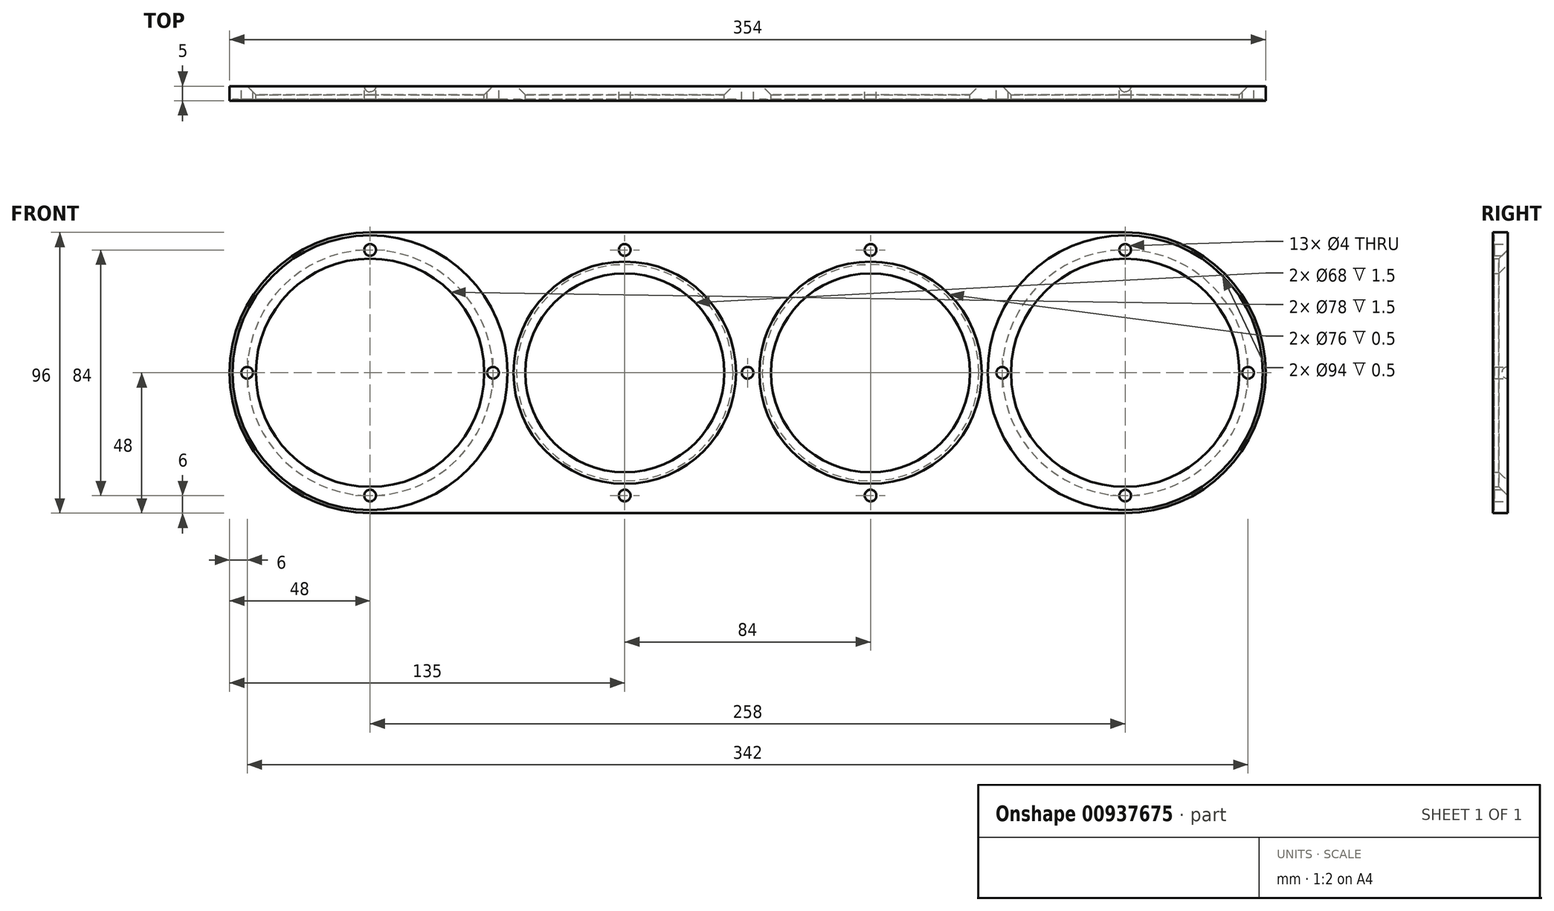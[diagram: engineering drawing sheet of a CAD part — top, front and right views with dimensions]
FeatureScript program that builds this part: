
annotation { "Feature Type Name" : "Feature", "Feature Type Description" : "" }
export const myFeature = defineFeature(function(context is Context, id is Id, definition is map)
    precondition{}
    {
        {
            var Q0;
            Q0=qCreatedBy(makeId("Front.planeOp"),FACE);
            var sketch = newSketch(context, id + "F0", { "sketchPlane" : qUnion([Q0])});
            skCircle(sketch, "E0", {"center": v(42, 0) * mm, "radius": 34 * mm});
            skCircle(sketch, "E1", {"center": v(129, 0) * mm, "radius": 39 * mm});
            skLineSegment(sketch, "E2", {"start": v(0, -113.77) * mm, "end": v(0, 113.17) * mm, "construction": true});
            skArc(sketch, "E3", {"start": v(129, 48) * mm, "mid": v(177, 0) * mm, "end": v(129, -48) * mm});
            skLineSegment(sketch, "E4", {"start": v(129, -48) * mm, "end": v(0, -48) * mm});
            skLineSegment(sketch, "E5", {"start": v(129, 48) * mm, "end": v(0, 48) * mm});
            skLineSegment(sketch, "E6.MirrorCS", {"start": v(-129, -48) * mm, "end": v(0, -48) * mm});
            skLineSegment(sketch, "E7.MirrorCS", {"start": v(-129, 48) * mm, "end": v(0, 48) * mm});
            skArc(sketch, "E8.MirrorCS", {"start": v(-129, 48) * mm, "mid": v(-177, 0) * mm, "end": v(-129, -48) * mm});
            skCircle(sketch, "E9.MirrorC", {"center": v(-129, 0) * mm, "radius": 39 * mm});
            skCircle(sketch, "E10.MirrorC", {"center": v(-42, 0) * mm, "radius": 34 * mm});
            skCircle(sketch, "E11", {"center": v(129, 42) * mm, "radius": 2 * mm});
            skCircle(sketch, "E12.1.0", {"center": v(87, 0) * mm, "radius": 2 * mm});
            skCircle(sketch, "E12.2.0", {"center": v(129, -42) * mm, "radius": 2 * mm});
            skCircle(sketch, "E12.3.0", {"center": v(171, 0) * mm, "radius": 2 * mm});
            skCircle(sketch, "E13.MirrorC", {"center": v(-171, 0) * mm, "radius": 2 * mm});
            skCircle(sketch, "E14.MirrorC", {"center": v(-129, 42) * mm, "radius": 2 * mm});
            skCircle(sketch, "E15.MirrorC", {"center": v(-129, -42) * mm, "radius": 2 * mm});
            skCircle(sketch, "E16.MirrorC", {"center": v(-87, 0) * mm, "radius": 2 * mm});
            skCircle(sketch, "E17", {"center": v(42, 42) * mm, "radius": 2 * mm});
            skCircle(sketch, "E18.1.0", {"center": v(42, -42) * mm, "radius": 2 * mm});
            skCircle(sketch, "E19.MirrorC", {"center": v(-42, 42) * mm, "radius": 2 * mm});
            skCircle(sketch, "E20.MirrorC", {"center": v(-42, -42) * mm, "radius": 2 * mm});
            skCircle(sketch, "E21", {"center": v(0, 0) * mm, "radius": 2 * mm});
            skSolve(sketch);
        }
        {
            var Q0;
            Q0=qSketchRegion(id+"F0",true);
            extrude(context, id + "F1", {"entities" : qUnion([Q0]), "depth" : 5 * mm, "offsetDistance" : 25 * mm});
        }
        {
            var Q0;
            Q0=makeQuery(id+"F1.opExtrude","CAP_FACE",FACE,{"disambiguationData":[OSD([sQuery(id+"F0.wireOp",EDGE,"E0"),sQuery(id+"F0.wireOp",EDGE,"E1"),sQuery(id+"F0.wireOp",EDGE,"E3"),sQuery(id+"F0.wireOp",EDGE,"E4"),sQuery(id+"F0.wireOp",EDGE,"E5"),sQuery(id+"F0.wireOp",EDGE,"E6.MirrorCS"),sQuery(id+"F0.wireOp",EDGE,"E7.MirrorCS"),sQuery(id+"F0.wireOp",EDGE,"E8.MirrorCS"),sQuery(id+"F0.wireOp",EDGE,"E9.MirrorC"),sQuery(id+"F0.wireOp",EDGE,"E10.MirrorC")])],"isStart":false});
            var sketch = newSketch(context, id + "F2", { "sketchPlane" : qUnion([Q0])});
            skCircle(sketch, "E22", {"center": v(42, 0) * mm, "radius": 38 * mm});
            skCircle(sketch, "E23.MirrorC", {"center": v(-42, 0) * mm, "radius": 38 * mm});
            skCircle(sketch, "E24", {"center": v(129, 0) * mm, "radius": 47 * mm});
            skCircle(sketch, "E25.MirrorC", {"center": v(-129, 0) * mm, "radius": 47 * mm});
            skSolve(sketch);
        }
        {
            var Q0;
            Q0 = qSketchRegion(id + "F2", true);
            extrude(context, id + "F3", {"entities" : qUnion([Q0]), "operationType" : NewBodyOperationType.REMOVE, "oppositeDirection" : true, "depth" : 0.5 * mm, "offsetDistance" : 25 * mm});
        }
        {
            var Q0;
            Q0=makeQuery(id+"F1.opExtrude","CAP_EDGE",EDGE,{"disambiguationData":[OSD([sQuery(id+"F0.wireOp",EDGE,"E9.MirrorC")])],"isStart":true});
            var Q1;
            Q1=makeQuery(id+"F1.opExtrude","CAP_EDGE",EDGE,{"disambiguationData":[OSD([sQuery(id+"F0.wireOp",EDGE,"E10.MirrorC")])],"isStart":true});
            var Q2;
            Q2=makeQuery(id+"F1.opExtrude","CAP_EDGE",EDGE,{"disambiguationData":[OSD([sQuery(id+"F0.wireOp",EDGE,"E0")])],"isStart":true});
            var Q3;
            Q3=makeQuery(id+"F1.opExtrude","CAP_EDGE",EDGE,{"disambiguationData":[OSD([sQuery(id+"F0.wireOp",EDGE,"E1")])],"isStart":true});
            chamfer(context, id + "F4", {"entities" : qUnion([Q0, Q1, Q2, Q3]), "width" : 3 * mm, "tangentPropagation" : true});
        }
    });
